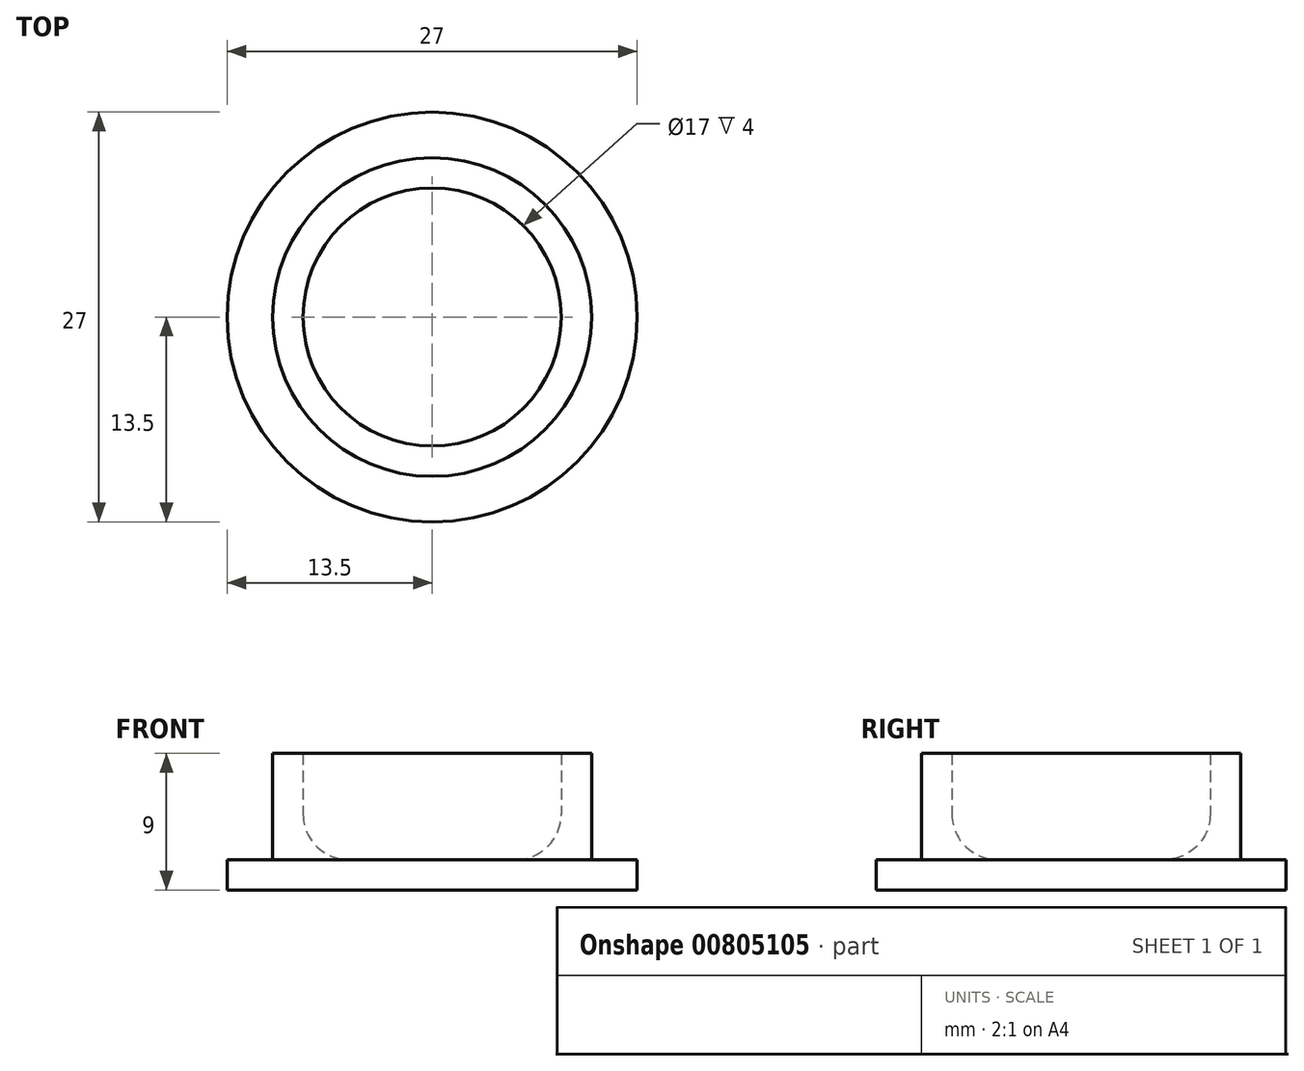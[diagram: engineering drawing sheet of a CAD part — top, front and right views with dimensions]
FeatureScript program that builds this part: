
annotation { "Feature Type Name" : "Feature", "Feature Type Description" : "" }
export const myFeature = defineFeature(function(context is Context, id is Id, definition is map)
    precondition{}
    {
        {
            var Q0;
            Q0=qCreatedBy(makeId("Top.planeOp"),FACE);
            var sketch = newSketch(context, id + "F0", { "sketchPlane" : qUnion([Q0])});
            skCircle(sketch, "E0", {"center": v(0, 0) * mm, "radius": 13.5 * mm});
            skSolve(sketch);
        }
        {
            var Q0;
            Q0=qSketchRegion(id+"F0",true);
            extrude(context, id + "F1", {"entities" : qUnion([Q0]), "depth" : 2 * mm, "offsetDistance" : 25 * mm});
        }
        {
            var Q0;
            Q0=makeQuery(id+"F1.opExtrude","CAP_FACE",FACE,{"disambiguationData":[OSD([sQuery(id+"F0.wireOp",EDGE,"E0")])],"isStart":false});
            var sketch = newSketch(context, id + "F2", { "sketchPlane" : qUnion([Q0])});
            skCircle(sketch, "E1", {"center": v(0, 0) * mm, "radius": 10.5 * mm});
            skCircle(sketch, "E2", {"center": v(0, 0) * mm, "radius": 8.5 * mm});
            skSolve(sketch);
        }
        {
            var Q0;
            Q0=makeQuery(id+"F2.imprint","IMPRINT",FACE,{"disambiguationData":[TD([[makeQuery(id+"F2.imprint","IMPRINT",EDGE,{"derivedFrom":sQuery(id+"F2.wireOp",EDGE,"E1")}),1.0]])]});
            extrude(context, id + "F3", {"entities" : qUnion([Q0]), "operationType" : NewBodyOperationType.ADD, "depth" : 7 * mm, "offsetDistance" : 25 * mm});
        }
        {
            var Q0;
            Q0=makeQuery(id+"F3.opExtrude","CAP_EDGE",EDGE,{"disambiguationData":[OSD([sQuery(id+"F2.wireOp",EDGE,"E2")])],"isStart":true});
            fillet(context, id + "F4", {"entities" : qUnion([Q0]), "radius" : 3 * mm, "tangentPropagation" : true, "allowEdgeOverflow" : false});
        }
    });
